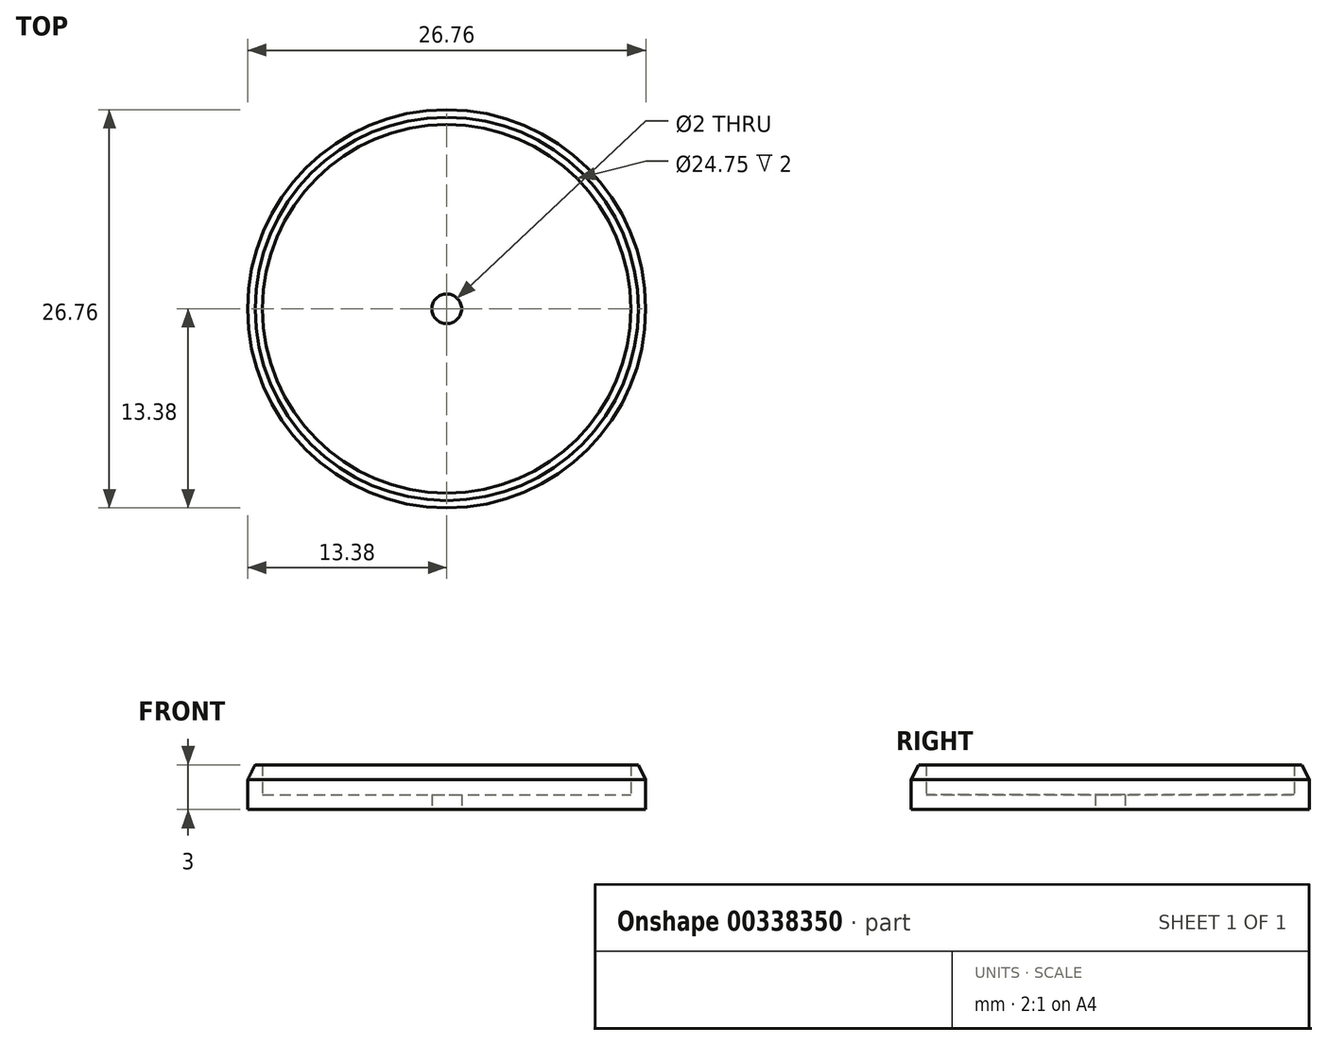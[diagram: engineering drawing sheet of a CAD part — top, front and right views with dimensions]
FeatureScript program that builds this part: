
annotation { "Feature Type Name" : "Feature", "Feature Type Description" : "" }
export const myFeature = defineFeature(function(context is Context, id is Id, definition is map)
    precondition{}
    {
        {
            var Q0;
            Q0=qCreatedBy(makeId("Front.planeOp"),FACE);
            var sketch = newSketch(context, id + "F0", { "sketchPlane" : qUnion([Q0])});
            skLineSegment(sketch, "E0", {"start": v(0, 0) * mm, "end": v(-1, 0) * mm, "construction": true});
            skLineSegment(sketch, "E1", {"start": v(-1, 0) * mm, "end": v(-13.38, 0) * mm});
            skLineSegment(sketch, "E2", {"start": v(-13.38, 0) * mm, "end": v(-13.38, 2) * mm});
            skLineSegment(sketch, "E3", {"start": v(-13.38, 2) * mm, "end": v(-12.88, 3) * mm});
            skLineSegment(sketch, "E4", {"start": v(-12.88, 3) * mm, "end": v(-12.38, 3) * mm});
            skLineSegment(sketch, "E5", {"start": v(-12.38, 3) * mm, "end": v(-12.38, 1) * mm});
            skLineSegment(sketch, "E6", {"start": v(-12.38, 1) * mm, "end": v(-1, 1) * mm});
            skLineSegment(sketch, "E7", {"start": v(-1, 1) * mm, "end": v(-1, 0) * mm});
            skLineSegment(sketch, "E8", {"start": v(0, 0) * mm, "end": v(0, 1) * mm, "construction": true});
            skSolve(sketch);
        }
        {
            var Q0;
            Q0 = qSketchRegion(id + "F0", true);
            var Q1;
            Q1=sQuery(id+"F0.wireOp",EDGE,"E8");
            revolve(context, id + "F1", {"entities" : qUnion([Q0]), "axis" : qUnion([Q1]), "revolveType" : RevolveType.FULL});
        }
    });
